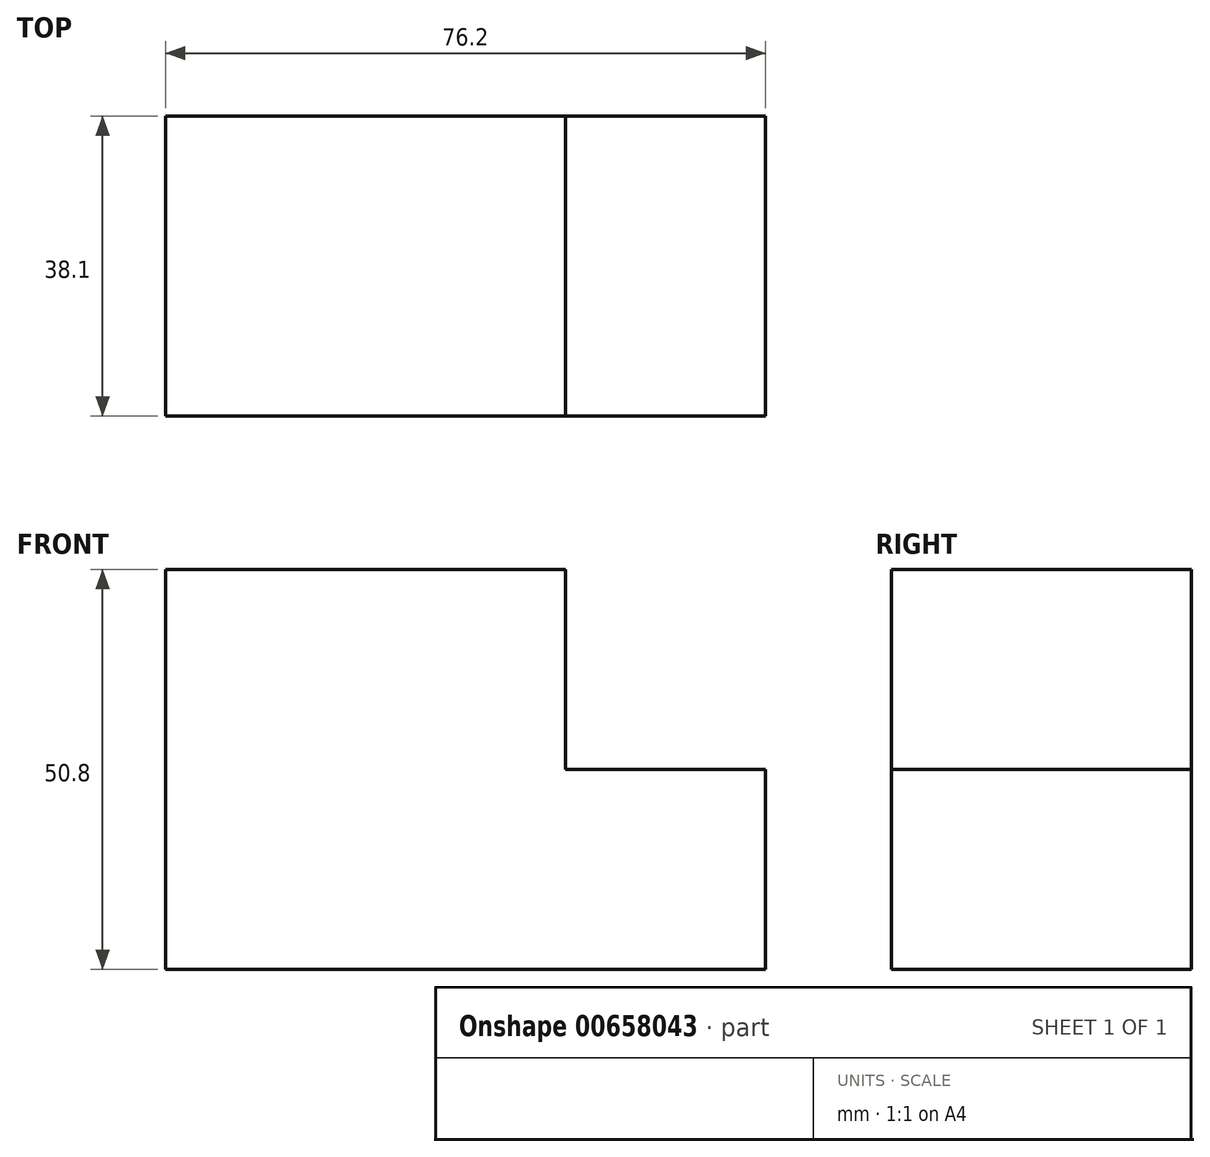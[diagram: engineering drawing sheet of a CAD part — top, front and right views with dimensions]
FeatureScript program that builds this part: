
annotation { "Feature Type Name" : "Feature", "Feature Type Description" : "" }
export const myFeature = defineFeature(function(context is Context, id is Id, definition is map)
    precondition{}
    {
        {
            var Q0;
            Q0=qCreatedBy(makeId("Front.planeOp"),FACE);
            var sketch = newSketch(context, id + "F0", { "sketchPlane" : qUnion([Q0])});
            skLineSegment(sketch, "E0", {"start": v(-32.94, -62.46) * mm, "end": v(43.26, -62.46) * mm});
            skLineSegment(sketch, "E1", {"start": v(43.26, -62.46) * mm, "end": v(43.26, -37.06) * mm});
            skLineSegment(sketch, "E2", {"start": v(43.26, -37.06) * mm, "end": v(17.86, -37.06) * mm});
            skLineSegment(sketch, "E3", {"start": v(17.86, -37.06) * mm, "end": v(17.86, -11.66) * mm});
            skLineSegment(sketch, "E4", {"start": v(17.86, -11.66) * mm, "end": v(-32.94, -11.66) * mm});
            skLineSegment(sketch, "E5", {"start": v(-32.94, -11.66) * mm, "end": v(-32.94, -62.46) * mm});
            skSolve(sketch);
        }
        {
            var Q0;
            Q0=makeQuery(id+"F0.imprint","IMPRINT",FACE,{"disambiguationData":[TD([[makeQuery(id+"F0.imprint","IMPRINT",EDGE,{"derivedFrom":sQuery(id+"F0.wireOp",EDGE,"E0")}),1.0]])]});
            extrude(context, id + "F1", {"entities" : qUnion([Q0]), "depth" : 38.1 * mm, "offsetDistance" : 25.4 * mm});
        }
    });
